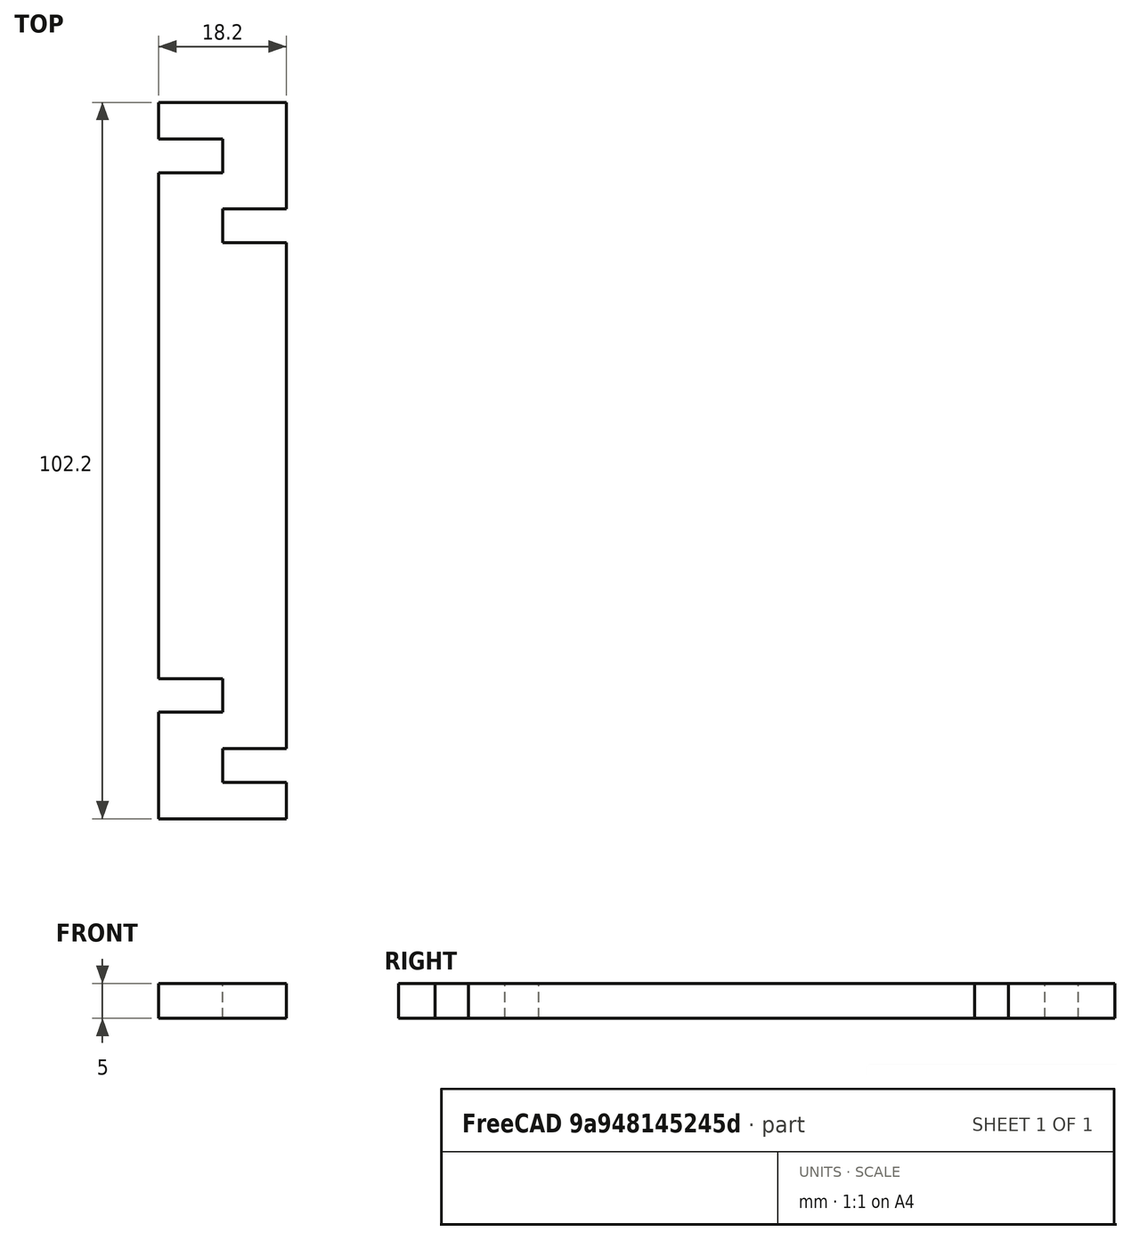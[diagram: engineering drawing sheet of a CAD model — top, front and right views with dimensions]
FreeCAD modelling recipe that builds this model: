
FCSTD DOCUMENT  (FreeCAD 0.16R6707 (Git))
Label: AssemblerWireMK2
License: All rights reserved
LicenseURL: http://en.wikipedia.org/wiki/All_rights_reserved
objects: Sketcher::SketchObject×1, PartDesign::Pad×1
note: 3 computed .brp shape members not serialized (recipe doc carries the construction recipe); baked Part::Feature solids carry a one-line shape summary decoded from their .brp

FEATURE [Sketcher::SketchObject] Sketch
  sketch-geometry (20):
    g0: LineSegment StartX=-9.1 StartY=51.1 StartZ=0 EndX=9.1 EndY=51.1 EndZ=0
    g1: LineSegment StartX=9.1 StartY=51.1 StartZ=0 EndX=9.1 EndY=35.9 EndZ=0
    g2: LineSegment StartX=9.1 StartY=35.9 StartZ=0 EndX=0 EndY=35.9 EndZ=0
    g3: LineSegment StartX=0 StartY=35.9 StartZ=0 EndX=0 EndY=31.1 EndZ=0
    g4: LineSegment StartX=0 StartY=31.1 StartZ=0 EndX=9.1 EndY=31.1 EndZ=0
    g5: LineSegment StartX=9.1 StartY=31.1 StartZ=0 EndX=9.1 EndY=-41.1 EndZ=0
    g6: LineSegment StartX=9.1 StartY=-41.1 StartZ=0 EndX=0 EndY=-41.1 EndZ=0
    g7: LineSegment StartX=0 StartY=-41.1 StartZ=0 EndX=0 EndY=-45.9 EndZ=0
    g8: LineSegment StartX=0 StartY=-45.9 StartZ=0 EndX=9.1 EndY=-45.9 EndZ=0
    g9: LineSegment StartX=9.1 StartY=-45.9 StartZ=0 EndX=9.1 EndY=-51.1 EndZ=0
    g10: LineSegment StartX=9.1 StartY=-51.1 StartZ=0 EndX=-9.1 EndY=-51.1 EndZ=0
    g11: LineSegment StartX=-9.1 StartY=-51.1 StartZ=0 EndX=-9.1 EndY=-35.9 EndZ=0
    g12: LineSegment StartX=-9.1 StartY=-35.9 StartZ=0 EndX=0 EndY=-35.9 EndZ=0
    g13: LineSegment StartX=0 StartY=-35.9 StartZ=0 EndX=0 EndY=-31.1 EndZ=0
    g14: LineSegment StartX=0 StartY=-31.1 StartZ=0 EndX=-9.1 EndY=-31.1 EndZ=0
    g15: LineSegment StartX=-9.1 StartY=-31.1 StartZ=0 EndX=-9.1 EndY=41.1 EndZ=0
    g16: LineSegment StartX=-9.1 StartY=41.1 StartZ=0 EndX=0 EndY=41.1 EndZ=0
    g17: LineSegment StartX=0 StartY=41.1 StartZ=0 EndX=0 EndY=45.9 EndZ=0
    g18: LineSegment StartX=0 StartY=45.9 StartZ=0 EndX=-9.1 EndY=45.9 EndZ=0
    g19: LineSegment StartX=-9.1 StartY=45.9 StartZ=0 EndX=-9.1 EndY=51.1 EndZ=0
  constraints (62):
    c: Horizontal(g0)
    c: Coincident(g0,g1)
    c: Vertical(g1)
    c: Coincident(g1,g2)
    c: PointOnObject(g2,g-2)
    c: Horizontal(g2)
    c: Coincident(g2,g3)
    c: Coincident(g3,g4)
    c: Horizontal(g4)
    c: Coincident(g4,g5)
    c: Vertical(g5)
    c: Coincident(g5,g6)
    c: PointOnObject(g6,g-2)
    c: Horizontal(g6)
    c: Coincident(g6,g7)
    c: PointOnObject(g7,g-2)
    c: Coincident(g7,g8)
    c: Horizontal(g8)
    c: Coincident(g8,g9)
    c: Vertical(g9)
    c: Coincident(g9,g10)
    c: Coincident(g10,g11)
    c: Vertical(g11)
    c: Coincident(g11,g12)
    c: Horizontal(g12)
    c: Coincident(g12,g13)
    c: Coincident(g13,g14)
    c: Coincident(g14,g15)
    c: Vertical(g15)
    c: Coincident(g15,g16)
    c: PointOnObject(g16,g-2)
    c: Horizontal(g16)
    c: Coincident(g16,g17)
    c: Vertical(g17)
    c: Coincident(g17,g18)
    c: Horizontal(g18)
    c: Coincident(g18,g19)
    c: Coincident(g19,g0)
    c: Vertical(g19)
    c: Horizontal(g14)
    c: Symmetric(g3,g13,g-1)
    c: Symmetric(g16,g6,g-1)
    c: Symmetric(g0,g0,g-2)
    c: Symmetric(g9,g10,g-2)
    c: Symmetric(g10,g0,g-1)
    c: Equal(g17,g3)
    c: Equal(g3,g13)
    c: Equal(g13,g7)
    c: Equal(g18,g16)
    c: Equal(g16,g2)
    c: Equal(g2,g4)
    c: Equal(g4,g14)
    c: Equal(g14,g12)
    c: Equal(g12,g6)
    c: Equal(g6,g8)
    c: DistanceY(g13,g3) = 62.2
    c: DistanceY(g13,g13) = 4.8
    c: DistanceY(g9,g9) = 5.2
    c: Equal(g9,g19)
    c: DistanceX(g0,g0) = 18.2
    c: DistanceY(g6,g12) = 5.2
    c: DistanceY(g9,g0) = 102.2
FEATURE [PartDesign::Pad] Pad
  Length = 5
  Length2 = 100
  Sketch = -> Sketch
  Type = 0
